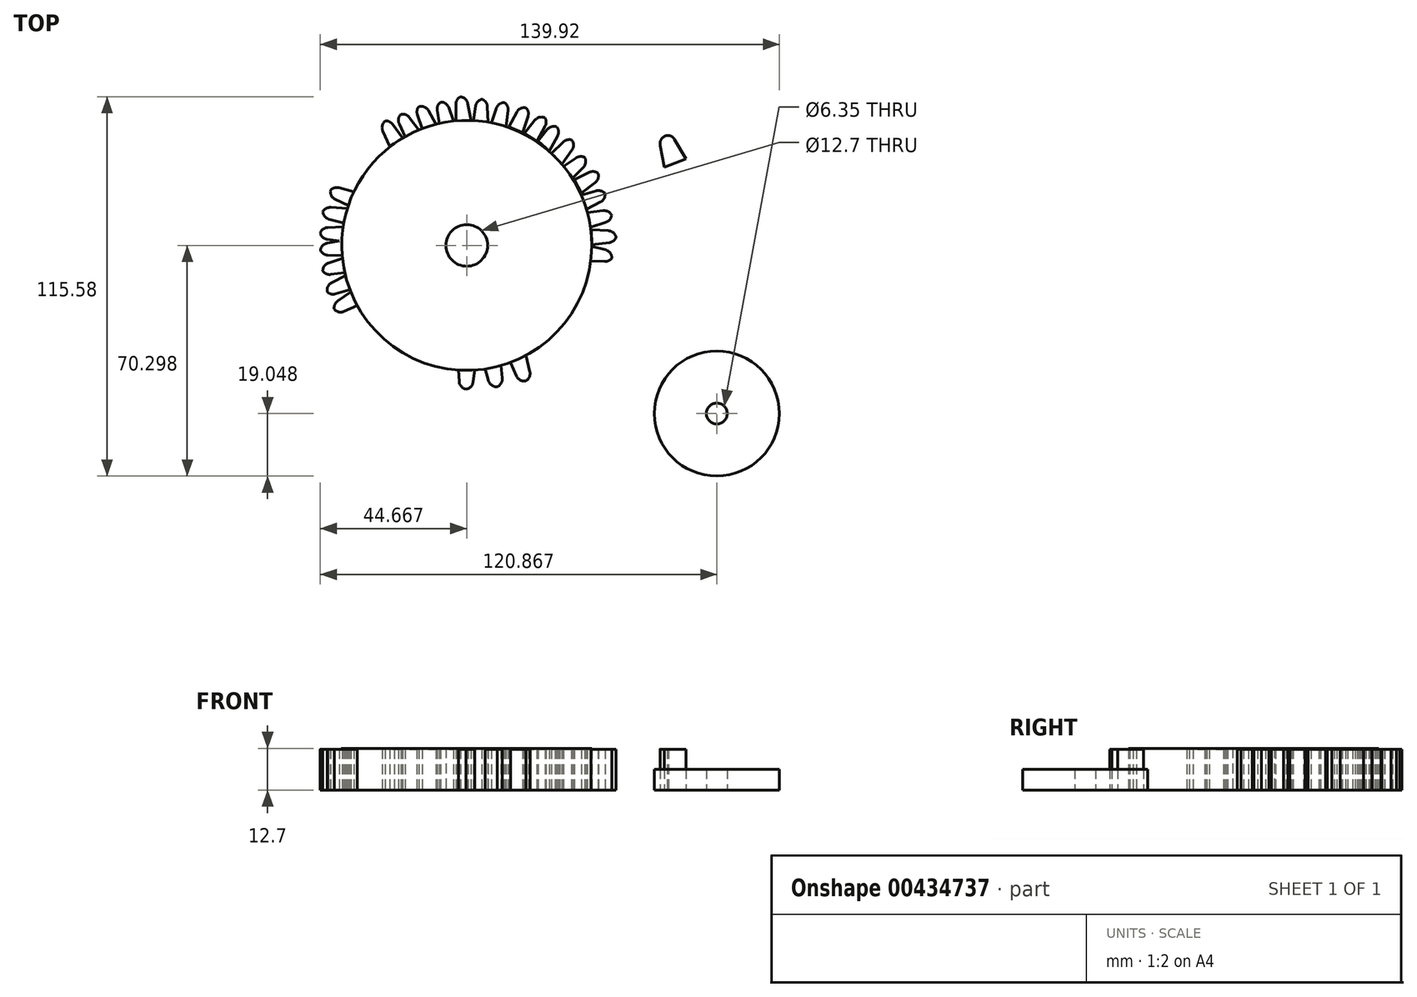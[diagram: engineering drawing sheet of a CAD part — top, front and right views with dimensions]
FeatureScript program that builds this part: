
annotation { "Feature Type Name" : "Feature", "Feature Type Description" : "" }
export const myFeature = defineFeature(function(context is Context, id is Id, definition is map)
    precondition{}
    {
        {
            var Q0;
            Q0=qCreatedBy(makeId("Top.planeOp"),FACE);
            var sketch = newSketch(context, id + "F0", { "sketchPlane" : qUnion([Q0])});
            skCircle(sketch, "E0", {"center": v(-39.08, 21.94) * mm, "radius": 38.1 * mm});
            skCircle(sketch, "E1", {"center": v(-39.08, 21.94) * mm, "radius": 6.35 * mm});
            skSolve(sketch);
        }
        {
            var Q0;
            Q0=makeQuery(id+"F0.imprint","IMPRINT",FACE,{"disambiguationData":[TD([[makeQuery(id+"F0.imprint","IMPRINT",EDGE,{"derivedFrom":sQuery(id+"F0.wireOp",EDGE,"E0")}),1.0]])]});
            extrude(context, id + "F1", {"entities" : qUnion([Q0]), "depth" : 12.7 * mm});
        }
        {
            var Q0;
            Q0=qCreatedBy(makeId("Top.planeOp"),FACE);
            var sketch = newSketch(context, id + "F2", { "sketchPlane" : qUnion([Q0])});
            skCircle(sketch, "E2", {"center": v(37.12, -29.31) * mm, "radius": 19.05 * mm});
            skCircle(sketch, "E3", {"center": v(37.12, -29.31) * mm, "radius": 3.18 * mm});
            skSolve(sketch);
        }
        {
            var Q0;
            Q0=makeQuery(id+"F2.imprint","IMPRINT",FACE,{"disambiguationData":[TD([[makeQuery(id+"F2.imprint","IMPRINT",EDGE,{"derivedFrom":sQuery(id+"F2.wireOp",EDGE,"E2")}),1.0]])]});
            extrude(context, id + "F3", {"entities" : qUnion([Q0]), "depth" : 6.35 * mm});
        }
        {
            var Q0;
            Q0=qCreatedBy(makeId("Top.planeOp"),FACE);
            var sketch = newSketch(context, id + "F4", { "sketchPlane" : qUnion([Q0])});
            skLineSegment(sketch, "E4", {"start": v(-35.3, 66.23) * mm, "end": v(-34.44, 66.16) * mm});
            skLineSegment(sketch, "E5", {"start": v(-32.8, 64.2) * mm, "end": v(-32.6, 58.88) * mm});
            skLineSegment(sketch, "E6", {"start": v(-32.6, 58.88) * mm, "end": v(-37.18, 59.33) * mm});
            skLineSegment(sketch, "E7", {"start": v(-37.18, 59.33) * mm, "end": v(-36.4, 64.4) * mm});
            skPoint(sketch, "E8.visualSharp", {"position": v(-36.84, 66.37) * mm});
            skArc(sketch, "E8.filletArc", {"start": v(-33.64, 66.57) * mm, "mid": v(-35.45, 66.03) * mm, "end": v(-36.4, 64.4) * mm});
            skPoint(sketch, "E9.visualSharp", {"position": v(-33.04, 66.03) * mm});
            skArc(sketch, "E9.filletArc", {"start": v(-32.8, 64.2) * mm, "mid": v(-33.5, 65.87) * mm, "end": v(-35.14, 66.66) * mm});
            skLineSegment(sketch, "E10.MirrorCS", {"start": v(-36.5, -14.4) * mm, "end": v(-41.75, -14.4) * mm});
            skLineSegment(sketch, "E11.MirrorCS", {"start": v(-37.17, -19.67) * mm, "end": v(-36.5, -14.4) * mm});
            skLineSegment(sketch, "E12.MirrorCS", {"start": v(-41.75, -14.4) * mm, "end": v(-41.42, -19.52) * mm});
            skArc(sketch, "E13.MirrorCS", {"start": v(-38.85, -21.92) * mm, "mid": v(-40.6, -21.22) * mm, "end": v(-41.42, -19.52) * mm});
            skArc(sketch, "E14.MirrorCS", {"start": v(-37.17, -19.67) * mm, "mid": v(-38.02, -21.28) * mm, "end": v(-39.71, -21.92) * mm});
            skLineSegment(sketch, "E15", {"start": v(22.03, 55.48) * mm, "end": v(22.39, 55.48) * mm});
            skLineSegment(sketch, "E16", {"start": v(24.23, 54.24) * mm, "end": v(27.77, 48.34) * mm});
            skLineSegment(sketch, "E17", {"start": v(27.77, 48.34) * mm, "end": v(21.15, 45.8) * mm});
            skLineSegment(sketch, "E18", {"start": v(21.15, 45.8) * mm, "end": v(19.87, 52.43) * mm});
            skPoint(sketch, "E19.visualSharp", {"position": v(19.27, 55.48) * mm});
            skArc(sketch, "E19.filletArc", {"start": v(22.39, 55.48) * mm, "mid": v(20.4, 54.55) * mm, "end": v(19.87, 52.43) * mm});
            skPoint(sketch, "E20.visualSharp", {"position": v(23.48, 55.48) * mm});
            skArc(sketch, "E20.filletArc", {"start": v(24.23, 54.24) * mm, "mid": v(23.3, 55.15) * mm, "end": v(22.03, 55.48) * mm});
            skLineSegment(sketch, "E21", {"start": v(-28.47, 65.32) * mm, "end": v(-27.63, 65.13) * mm});
            skLineSegment(sketch, "E22", {"start": v(-26.48, 63) * mm, "end": v(-27.17, 57.73) * mm});
            skLineSegment(sketch, "E23", {"start": v(-27.17, 57.73) * mm, "end": v(-31.65, 58.88) * mm});
            skLineSegment(sketch, "E24", {"start": v(-31.65, 58.88) * mm, "end": v(-30.03, 63.75) * mm});
            skPoint(sketch, "E25.visualSharp", {"position": v(-29.98, 65.66) * mm});
            skArc(sketch, "E25.filletArc", {"start": v(-26.94, 65.43) * mm, "mid": v(-28.82, 65.2) * mm, "end": v(-30.03, 63.75) * mm});
            skPoint(sketch, "E26.visualSharp", {"position": v(-26.26, 64.82) * mm});
            skArc(sketch, "E26.filletArc", {"start": v(-26.48, 63) * mm, "mid": v(-26.9, 64.78) * mm, "end": v(-28.37, 65.83) * mm});
            skLineSegment(sketch, "E27", {"start": v(-21.5, 63.19) * mm, "end": v(-20.68, 62.9) * mm});
            skLineSegment(sketch, "E28", {"start": v(-20.42, 61.32) * mm, "end": v(-22.04, 56.25) * mm});
            skLineSegment(sketch, "E29", {"start": v(-22.04, 56.25) * mm, "end": v(-26.3, 58.08) * mm});
            skLineSegment(sketch, "E30", {"start": v(-26.3, 58.08) * mm, "end": v(-23.83, 62.6) * mm});
            skPoint(sketch, "E31.visualSharp", {"position": v(-22.95, 63.72) * mm});
            skArc(sketch, "E31.filletArc", {"start": v(-20.5, 63.7) * mm, "mid": v(-22.38, 63.8) * mm, "end": v(-23.83, 62.6) * mm});
            skPoint(sketch, "E32.visualSharp", {"position": v(-19.37, 62.42) * mm});
            skArc(sketch, "E32.filletArc", {"start": v(-20.42, 61.32) * mm, "mid": v(-20.52, 63.14) * mm, "end": v(-21.78, 64.43) * mm});
            skLineSegment(sketch, "E33.MirrorCS", {"start": v(-21.04, -11.39) * mm, "end": v(-25.98, -13.19) * mm});
            skLineSegment(sketch, "E34.MirrorCS", {"start": v(-19.87, -16.58) * mm, "end": v(-21.04, -11.39) * mm});
            skLineSegment(sketch, "E35.MirrorCS", {"start": v(-25.98, -13.19) * mm, "end": v(-23.91, -17.89) * mm});
            skPoint(sketch, "E36.MirrorP", {"position": v(-22.95, -20.1) * mm});
            skArc(sketch, "E37.MirrorCS", {"start": v(-20.68, -19.27) * mm, "mid": v(-22.57, -19.22) * mm, "end": v(-23.91, -17.89) * mm});
            skArc(sketch, "E38.MirrorCS", {"start": v(-19.87, -16.58) * mm, "mid": v(-20.12, -18.38) * mm, "end": v(-21.5, -19.56) * mm});
            skLineSegment(sketch, "E39.MirrorCS", {"start": v(-28.77, -13.24) * mm, "end": v(-33.9, -14.4) * mm});
            skLineSegment(sketch, "E40.MirrorCS", {"start": v(-33.9, -14.4) * mm, "end": v(-32.45, -19.32) * mm});
            skLineSegment(sketch, "E41.MirrorCS", {"start": v(-28.26, -18.54) * mm, "end": v(-28.77, -13.24) * mm});
            skArc(sketch, "E42.MirrorCS", {"start": v(-28.26, -18.54) * mm, "mid": v(-28.74, -20.3) * mm, "end": v(-30.26, -21.29) * mm});
            skArc(sketch, "E43.MirrorCS", {"start": v(-29.42, -21.1) * mm, "mid": v(-31.29, -20.8) * mm, "end": v(-32.45, -19.32) * mm});
            skLineSegment(sketch, "E44", {"start": v(-14.43, 59.39) * mm, "end": v(-13.73, 58.9) * mm});
            skLineSegment(sketch, "E45", {"start": v(-15.19, 58.33) * mm, "end": v(-17.67, 53.62) * mm});
            skLineSegment(sketch, "E46", {"start": v(-17.67, 53.62) * mm, "end": v(-21.55, 56.1) * mm});
            skLineSegment(sketch, "E47", {"start": v(-21.55, 56.1) * mm, "end": v(-18.33, 60.1) * mm});
            skPoint(sketch, "E48.visualSharp", {"position": v(-15.7, 60.27) * mm});
            skArc(sketch, "E48.filletArc", {"start": v(-14.86, 60.6) * mm, "mid": v(-16.7, 61.04) * mm, "end": v(-18.33, 60.1) * mm});
            skPoint(sketch, "E49.visualSharp", {"position": v(-12.58, 58.09) * mm});
            skArc(sketch, "E49.filletArc", {"start": v(-15.19, 58.33) * mm, "mid": v(-14.96, 60.13) * mm, "end": v(-15.99, 61.63) * mm});
            skLineSegment(sketch, "E50", {"start": v(-42.6, 66.02) * mm, "end": v(-41.75, 66.1) * mm});
            skLineSegment(sketch, "E51", {"start": v(-38.81, 65.23) * mm, "end": v(-37.73, 60.09) * mm});
            skLineSegment(sketch, "E52", {"start": v(-37.73, 60.09) * mm, "end": v(-42.34, 59.84) * mm});
            skLineSegment(sketch, "E53", {"start": v(-42.34, 59.84) * mm, "end": v(-42.41, 64.91) * mm});
            skPoint(sketch, "E54.visualSharp", {"position": v(-44.12, 65.9) * mm});
            skArc(sketch, "E54.filletArc", {"start": v(-40.09, 67.48) * mm, "mid": v(-41.76, 66.66) * mm, "end": v(-42.41, 64.91) * mm});
            skPoint(sketch, "E55.visualSharp", {"position": v(-40.37, 66.2) * mm});
            skArc(sketch, "E55.filletArc", {"start": v(-38.81, 65.23) * mm, "mid": v(-39.77, 66.74) * mm, "end": v(-41.5, 67.23) * mm});
            skLineSegment(sketch, "E56", {"start": v(-49.7, 65.98) * mm, "end": v(-48.86, 66.16) * mm});
            skLineSegment(sketch, "E57", {"start": v(-44.58, 63.95) * mm, "end": v(-42.78, 59.01) * mm});
            skLineSegment(sketch, "E58", {"start": v(-42.78, 59.01) * mm, "end": v(-47.28, 58.17) * mm});
            skLineSegment(sketch, "E59", {"start": v(-47.28, 58.17) * mm, "end": v(-48.09, 63.18) * mm});
            skPoint(sketch, "E60.visualSharp", {"position": v(-51.18, 65.64) * mm});
            skArc(sketch, "E60.filletArc", {"start": v(-46.15, 66.05) * mm, "mid": v(-47.69, 65) * mm, "end": v(-48.09, 63.18) * mm});
            skPoint(sketch, "E61.visualSharp", {"position": v(-47.51, 66.47) * mm});
            skArc(sketch, "E61.filletArc", {"start": v(-44.58, 63.95) * mm, "mid": v(-45.75, 65.3) * mm, "end": v(-47.52, 65.55) * mm});
            skLineSegment(sketch, "E62", {"start": v(-55.81, 62.91) * mm, "end": v(-55.02, 63.2) * mm});
            skLineSegment(sketch, "E63", {"start": v(-50.75, 63.05) * mm, "end": v(-48.18, 58.47) * mm});
            skLineSegment(sketch, "E64", {"start": v(-48.18, 58.47) * mm, "end": v(-52.55, 57.03) * mm});
            skLineSegment(sketch, "E65", {"start": v(-52.55, 57.03) * mm, "end": v(-54.15, 61.84) * mm});
            skPoint(sketch, "E66.visualSharp", {"position": v(-57.25, 62.4) * mm});
            skArc(sketch, "E66.filletArc", {"start": v(-52.7, 64.98) * mm, "mid": v(-54.05, 63.7) * mm, "end": v(-54.15, 61.84) * mm});
            skPoint(sketch, "E67.visualSharp", {"position": v(-53.72, 63.68) * mm});
            skArc(sketch, "E67.filletArc", {"start": v(-50.75, 63.05) * mm, "mid": v(-52.12, 64.2) * mm, "end": v(-53.91, 64.15) * mm});
            skLineSegment(sketch, "E68", {"start": v(-62.7, 59.48) * mm, "end": v(-61.97, 59.9) * mm});
            skLineSegment(sketch, "E69", {"start": v(-56.56, 60.92) * mm, "end": v(-53.44, 56.7) * mm});
            skLineSegment(sketch, "E70", {"start": v(-53.44, 56.7) * mm, "end": v(-57.76, 54.9) * mm});
            skLineSegment(sketch, "E71", {"start": v(-57.76, 54.9) * mm, "end": v(-59.69, 58.95) * mm});
            skPoint(sketch, "E72.visualSharp", {"position": v(-64.04, 58.73) * mm});
            skArc(sketch, "E72.filletArc", {"start": v(-59.13, 61.9) * mm, "mid": v(-59.89, 60.51) * mm, "end": v(-59.69, 58.95) * mm});
            skArc(sketch, "E73.filletArc", {"start": v(-56.56, 60.92) * mm, "mid": v(-58.06, 61.9) * mm, "end": v(-59.83, 61.63) * mm});
            skPoint(sketch, "E74", {"position": v(-58.06, 61.9) * mm});
            skLineSegment(sketch, "E75", {"start": v(-76.83, 45.84) * mm, "end": v(-76.38, 46.56) * mm});
            skLineSegment(sketch, "E76", {"start": v(-81.45, 27.4) * mm, "end": v(-76.13, 27.64) * mm});
            skLineSegment(sketch, "E77", {"start": v(-76.13, 27.64) * mm, "end": v(-76.55, 23.05) * mm});
            skLineSegment(sketch, "E78", {"start": v(-76.55, 23.05) * mm, "end": v(-81.64, 23.8) * mm});
            skPoint(sketch, "E79.visualSharp", {"position": v(-77.65, 44.52) * mm});
            skArc(sketch, "E79.filletArc", {"start": v(-83.82, 26.55) * mm, "mid": v(-83.27, 24.74) * mm, "end": v(-81.64, 23.8) * mm});
            skPoint(sketch, "E80.visualSharp", {"position": v(-75.64, 47.76) * mm});
            skArc(sketch, "E80.filletArc", {"start": v(-81.45, 27.4) * mm, "mid": v(-83.12, 26.69) * mm, "end": v(-83.9, 25.05) * mm});
            skLineSegment(sketch, "E81", {"start": v(-72.93, 51.51) * mm, "end": v(-72.38, 52.17) * mm});
            skLineSegment(sketch, "E82", {"start": v(-80.54, 33.53) * mm, "end": v(-75.23, 33.12) * mm});
            skLineSegment(sketch, "E83", {"start": v(-75.23, 33.12) * mm, "end": v(-76.13, 28.58) * mm});
            skLineSegment(sketch, "E84", {"start": v(-76.13, 28.58) * mm, "end": v(-81.09, 29.94) * mm});
            skPoint(sketch, "E85.visualSharp", {"position": v(-73.92, 50.32) * mm});
            skArc(sketch, "E85.filletArc", {"start": v(-82.92, 32.93) * mm, "mid": v(-82.6, 31.07) * mm, "end": v(-81.09, 29.94) * mm});
            skPoint(sketch, "E86.visualSharp", {"position": v(-71.49, 53.25) * mm});
            skArc(sketch, "E86.filletArc", {"start": v(-80.54, 33.53) * mm, "mid": v(-82.28, 33.02) * mm, "end": v(-83.25, 31.48) * mm});
            skLineSegment(sketch, "E87", {"start": v(-80.22, 38.77) * mm, "end": v(-79.97, 39.6) * mm});
            skLineSegment(sketch, "E88", {"start": v(-78.12, 39.49) * mm, "end": v(-72.97, 38.14) * mm});
            skLineSegment(sketch, "E89", {"start": v(-72.97, 38.14) * mm, "end": v(-74.57, 33.8) * mm});
            skLineSegment(sketch, "E90", {"start": v(-74.57, 33.8) * mm, "end": v(-79.2, 36.01) * mm});
            skPoint(sketch, "E91.visualSharp", {"position": v(-80.67, 37.3) * mm});
            skArc(sketch, "E91.filletArc", {"start": v(-80.48, 39.29) * mm, "mid": v(-80.5, 37.4) * mm, "end": v(-79.2, 36.01) * mm});
            skPoint(sketch, "E92.visualSharp", {"position": v(-79.57, 40.94) * mm});
            skArc(sketch, "E92.filletArc", {"start": v(-78.12, 39.49) * mm, "mid": v(-79.93, 39.3) * mm, "end": v(-81.15, 37.96) * mm});
            skLineSegment(sketch, "E93", {"start": v(-61.28, 61.34) * mm, "end": v(-60.53, 61.74) * mm});
            skLineSegment(sketch, "E94", {"start": v(-61.67, 58.84) * mm, "end": v(-58.6, 54.5) * mm});
            skLineSegment(sketch, "E95", {"start": v(-58.6, 54.5) * mm, "end": v(-62.57, 52.16) * mm});
            skLineSegment(sketch, "E96", {"start": v(-62.57, 52.16) * mm, "end": v(-64.68, 56.84) * mm});
            skPoint(sketch, "E97.visualSharp", {"position": v(-62.65, 60.61) * mm});
            skArc(sketch, "E97.filletArc", {"start": v(-63.55, 60.16) * mm, "mid": v(-64.78, 58.72) * mm, "end": v(-64.68, 56.84) * mm});
            skPoint(sketch, "E98.visualSharp", {"position": v(-59.29, 62.4) * mm});
            skArc(sketch, "E98.filletArc", {"start": v(-61.67, 58.84) * mm, "mid": v(-63.18, 59.85) * mm, "end": v(-64.98, 59.62) * mm});
            skLineSegment(sketch, "E99", {"start": v(-83.05, 19.12) * mm, "end": v(-83.1, 19.97) * mm});
            skLineSegment(sketch, "E100", {"start": v(-81.64, 22.6) * mm, "end": v(-76.46, 23.5) * mm});
            skLineSegment(sketch, "E101", {"start": v(-76.46, 23.5) * mm, "end": v(-76.37, 18.9) * mm});
            skLineSegment(sketch, "E102", {"start": v(-76.37, 18.9) * mm, "end": v(-81.44, 18.98) * mm});
            skPoint(sketch, "E103.visualSharp", {"position": v(-80.53, 37.82) * mm});
            skArc(sketch, "E103.filletArc", {"start": v(-83.93, 21.4) * mm, "mid": v(-83.16, 19.7) * mm, "end": v(-81.44, 18.98) * mm});
            skPoint(sketch, "E104.visualSharp", {"position": v(-83.16, 21.35) * mm});
            skArc(sketch, "E104.filletArc", {"start": v(-81.64, 22.6) * mm, "mid": v(-83.18, 21.68) * mm, "end": v(-83.73, 19.98) * mm});
            skLineSegment(sketch, "E105", {"start": v(-83.13, 32.89) * mm, "end": v(-82.92, 33.7) * mm});
            skLineSegment(sketch, "E106", {"start": v(-81.21, 16.6) * mm, "end": v(-76.22, 18.24) * mm});
            skLineSegment(sketch, "E107", {"start": v(-76.22, 18.24) * mm, "end": v(-75.53, 13.7) * mm});
            skLineSegment(sketch, "E108", {"start": v(-75.53, 13.7) * mm, "end": v(-80.56, 13.07) * mm});
            skPoint(sketch, "E109.visualSharp", {"position": v(-83.5, 31.4) * mm});
            skArc(sketch, "E109.filletArc", {"start": v(-83.36, 15.1) * mm, "mid": v(-82.36, 13.54) * mm, "end": v(-80.56, 13.07) * mm});
            skPoint(sketch, "E110.visualSharp", {"position": v(-82.58, 35.05) * mm});
            skArc(sketch, "E110.filletArc", {"start": v(-81.21, 16.6) * mm, "mid": v(-82.6, 15.49) * mm, "end": v(-82.91, 13.72) * mm});
            skLineSegment(sketch, "E111", {"start": v(-83.17, 26.04) * mm, "end": v(-83.07, 26.88) * mm});
            skLineSegment(sketch, "E112", {"start": v(-80.26, 10.6) * mm, "end": v(-75.6, 13.02) * mm});
            skLineSegment(sketch, "E113", {"start": v(-75.6, 13.02) * mm, "end": v(-74.3, 8.6) * mm});
            skLineSegment(sketch, "E114", {"start": v(-74.3, 8.6) * mm, "end": v(-79.17, 7.16) * mm});
            skPoint(sketch, "E115.visualSharp", {"position": v(-83.35, 24.52) * mm});
            skArc(sketch, "E115.filletArc", {"start": v(-82.26, 8.72) * mm, "mid": v(-81.02, 7.33) * mm, "end": v(-79.17, 7.16) * mm});
            skPoint(sketch, "E116.visualSharp", {"position": v(-82.9, 28.25) * mm});
            skArc(sketch, "E116.filletArc", {"start": v(-80.26, 10.6) * mm, "mid": v(-81.46, 9.27) * mm, "end": v(-81.47, 7.48) * mm});
            skLineSegment(sketch, "E117", {"start": v(-83.23, 18.33) * mm, "end": v(-83.26, 19.18) * mm});
            skLineSegment(sketch, "E118", {"start": v(-78.42, 5) * mm, "end": v(-74.1, 7.97) * mm});
            skLineSegment(sketch, "E119", {"start": v(-74.1, 7.97) * mm, "end": v(-72.45, 3.6) * mm});
            skLineSegment(sketch, "E120", {"start": v(-72.45, 3.6) * mm, "end": v(-76.56, 1.8) * mm});
            skPoint(sketch, "E121.visualSharp", {"position": v(-83.17, 16.81) * mm});
            skArc(sketch, "E121.filletArc", {"start": v(-79.48, 2.46) * mm, "mid": v(-78.13, 1.65) * mm, "end": v(-76.56, 1.8) * mm});
            skArc(sketch, "E122.filletArc", {"start": v(-78.42, 5) * mm, "mid": v(-79.44, 3.52) * mm, "end": v(-79.24, 1.74) * mm});
            skPoint(sketch, "E123", {"position": v(-83.28, 23.57) * mm});
            skLineSegment(sketch, "E124.0", {"start": v(-83.76, 22.62) * mm, "end": v(-83.28, 23.57) * mm, "construction": true});
            skLineSegment(sketch, "E125.0", {"start": v(-69.32, 44.87) * mm, "end": v(-69.02, 45.47) * mm, "construction": true});
            skLineSegment(sketch, "E126", {"start": v(2.46, 38.33) * mm, "end": v(2.76, 37.52) * mm});
            skLineSegment(sketch, "E127", {"start": v(1.68, 35.2) * mm, "end": v(-3.04, 32.75) * mm});
            skLineSegment(sketch, "E128", {"start": v(-3.04, 32.75) * mm, "end": v(-4.6, 37.1) * mm});
            skLineSegment(sketch, "E129", {"start": v(-4.6, 37.1) * mm, "end": v(0.34, 38.55) * mm});
            skPoint(sketch, "E130.visualSharp", {"position": v(1.92, 39.78) * mm});
            skArc(sketch, "E130.filletArc", {"start": v(3.47, 36.98) * mm, "mid": v(2.22, 38.38) * mm, "end": v(0.34, 38.55) * mm});
            skPoint(sketch, "E131.visualSharp", {"position": v(3.24, 36.2) * mm});
            skArc(sketch, "E131.filletArc", {"start": v(1.68, 35.2) * mm, "mid": v(2.9, 36.55) * mm, "end": v(2.91, 38.37) * mm});
            skLineSegment(sketch, "E132", {"start": v(4.54, 31.76) * mm, "end": v(4.73, 30.92) * mm});
            skLineSegment(sketch, "E133", {"start": v(3.3, 28.98) * mm, "end": v(-1.77, 27.35) * mm});
            skLineSegment(sketch, "E134", {"start": v(-1.77, 27.35) * mm, "end": v(-2.64, 31.9) * mm});
            skLineSegment(sketch, "E135", {"start": v(-2.64, 31.9) * mm, "end": v(2.46, 32.5) * mm});
            skPoint(sketch, "E136.visualSharp", {"position": v(4.2, 33.27) * mm});
            skArc(sketch, "E136.filletArc", {"start": v(5.29, 30.43) * mm, "mid": v(4.29, 32.03) * mm, "end": v(2.46, 32.5) * mm});
            skPoint(sketch, "E137.visualSharp", {"position": v(5.04, 29.55) * mm});
            skArc(sketch, "E137.filletArc", {"start": v(3.3, 28.98) * mm, "mid": v(4.72, 30.1) * mm, "end": v(5.04, 31.9) * mm});
            skLineSegment(sketch, "E138", {"start": v(5.59, 24.54) * mm, "end": v(5.67, 23.69) * mm});
            skLineSegment(sketch, "E139", {"start": v(4.36, 22.78) * mm, "end": v(-0.92, 22.09) * mm});
            skLineSegment(sketch, "E140", {"start": v(-0.92, 22.09) * mm, "end": v(-1.08, 26.71) * mm});
            skLineSegment(sketch, "E141", {"start": v(-1.08, 26.71) * mm, "end": v(4.05, 26.4) * mm});
            skPoint(sketch, "E142.visualSharp", {"position": v(5.45, 26.08) * mm});
            skArc(sketch, "E142.filletArc", {"start": v(6.47, 23.86) * mm, "mid": v(5.76, 25.61) * mm, "end": v(4.05, 26.4) * mm});
            skPoint(sketch, "E143.visualSharp", {"position": v(5.8, 22.3) * mm});
            skArc(sketch, "E143.filletArc", {"start": v(4.36, 22.78) * mm, "mid": v(5.96, 23.64) * mm, "end": v(6.59, 25.34) * mm});
            skLineSegment(sketch, "E144", {"start": v(5.16, 16.54) * mm, "end": v(5.01, 15.69) * mm});
            skLineSegment(sketch, "E145", {"start": v(2.9, 17) * mm, "end": v(-2.41, 17.24) * mm});
            skLineSegment(sketch, "E146", {"start": v(-2.41, 17.24) * mm, "end": v(-1.82, 21.81) * mm});
            skLineSegment(sketch, "E147", {"start": v(-1.82, 21.81) * mm, "end": v(3.18, 20.61) * mm});
            skPoint(sketch, "E148.visualSharp", {"position": v(5.42, 18.06) * mm});
            skArc(sketch, "E148.filletArc", {"start": v(5.1, 17.68) * mm, "mid": v(4.72, 19.53) * mm, "end": v(3.18, 20.61) * mm});
            skPoint(sketch, "E149.visualSharp", {"position": v(4.77, 14.3) * mm});
            skArc(sketch, "E149.filletArc", {"start": v(2.9, 17) * mm, "mid": v(4.63, 17.57) * mm, "end": v(5.55, 19.14) * mm});
            skLineSegment(sketch, "E150", {"start": v(-0.84, 44.84) * mm, "end": v(-0.42, 44.1) * mm});
            skLineSegment(sketch, "E151", {"start": v(0.05, 41.08) * mm, "end": v(-4.14, 37.92) * mm});
            skLineSegment(sketch, "E152", {"start": v(-4.14, 37.92) * mm, "end": v(-6.32, 41.98) * mm});
            skLineSegment(sketch, "E153", {"start": v(-6.32, 41.98) * mm, "end": v(-1.77, 44.2) * mm});
            skPoint(sketch, "E154.visualSharp", {"position": v(-1.6, 46.17) * mm});
            skArc(sketch, "E154.filletArc", {"start": v(1.54, 43.2) * mm, "mid": v(0.09, 44.35) * mm, "end": v(-1.77, 44.2) * mm});
            skPoint(sketch, "E155.visualSharp", {"position": v(0.27, 42.9) * mm});
            skArc(sketch, "E155.filletArc", {"start": v(0.05, 41.08) * mm, "mid": v(1, 42.6) * mm, "end": v(0.72, 44.36) * mm});
            skLineSegment(sketch, "E156", {"start": v(-3.9, 51.24) * mm, "end": v(-3.38, 50.58) * mm});
            skLineSegment(sketch, "E157", {"start": v(-3.56, 45.75) * mm, "end": v(-7.26, 42.02) * mm});
            skLineSegment(sketch, "E158", {"start": v(-7.26, 42.02) * mm, "end": v(-9.94, 45.74) * mm});
            skLineSegment(sketch, "E159", {"start": v(-9.94, 45.74) * mm, "end": v(-5.75, 48.6) * mm});
            skPoint(sketch, "E160.visualSharp", {"position": v(-4.85, 52.44) * mm});
            skArc(sketch, "E160.filletArc", {"start": v(-2.33, 48.07) * mm, "mid": v(-3.94, 49.01) * mm, "end": v(-5.75, 48.6) * mm});
            skPoint(sketch, "E161.visualSharp", {"position": v(-2.53, 49.48) * mm});
            skArc(sketch, "E161.filletArc", {"start": v(-3.56, 45.75) * mm, "mid": v(-2.83, 47.39) * mm, "end": v(-3.37, 49.1) * mm});
            skLineSegment(sketch, "E162", {"start": v(-9.28, 55.48) * mm, "end": v(-8.68, 54.88) * mm});
            skLineSegment(sketch, "E163", {"start": v(-7, 50.95) * mm, "end": v(-10.05, 46.67) * mm});
            skLineSegment(sketch, "E164", {"start": v(-10.05, 46.67) * mm, "end": v(-13.22, 50.02) * mm});
            skLineSegment(sketch, "E165", {"start": v(-13.22, 50.02) * mm, "end": v(-9.55, 53.52) * mm});
            skPoint(sketch, "E166.visualSharp", {"position": v(-10.37, 56.55) * mm});
            skArc(sketch, "E166.filletArc", {"start": v(-6.1, 53.54) * mm, "mid": v(-7.83, 54.21) * mm, "end": v(-9.55, 53.52) * mm});
            skPoint(sketch, "E167.visualSharp", {"position": v(-7.7, 53.9) * mm});
            skArc(sketch, "E167.filletArc", {"start": v(-7, 50.95) * mm, "mid": v(-6.55, 52.69) * mm, "end": v(-7.36, 54.28) * mm});
            skLineSegment(sketch, "E168", {"start": v(-15.37, 59.96) * mm, "end": v(-14.68, 59.47) * mm});
            skLineSegment(sketch, "E169", {"start": v(-11.4, 55.3) * mm, "end": v(-13.9, 50.68) * mm});
            skLineSegment(sketch, "E170", {"start": v(-13.9, 50.68) * mm, "end": v(-17.35, 53.82) * mm});
            skLineSegment(sketch, "E171", {"start": v(-17.35, 53.82) * mm, "end": v(-14.52, 57.3) * mm});
            skPoint(sketch, "E172.visualSharp", {"position": v(-16.61, 60.85) * mm});
            skArc(sketch, "E172.filletArc", {"start": v(-11.62, 58.04) * mm, "mid": v(-13.2, 58.14) * mm, "end": v(-14.52, 57.3) * mm});
            skArc(sketch, "E173.filletArc", {"start": v(-11.4, 55.3) * mm, "mid": v(-11.17, 57.08) * mm, "end": v(-12.16, 58.57) * mm});
            skPoint(sketch, "E174", {"position": v(-11.17, 57.08) * mm});
            skLineSegment(sketch, "E175.0", {"start": v(-11.62, 58.04) * mm, "end": v(-11.17, 57.08) * mm, "construction": true});
            skLineSegment(sketch, "E176.0", {"start": v(-3.04, 32.75) * mm, "end": v(-2.64, 31.9) * mm, "construction": true});
            skPoint(sketch, "E177", {"position": v(-39, 21.81) * mm});
            skLineSegment(sketch, "E178", {"start": v(-39, 21.81) * mm, "end": v(-92.89, 21.81) * mm});
            skLineSegment(sketch, "E179", {"start": v(-92.89, 21.81) * mm, "end": v(-39, 21.81) * mm});
            skLineSegment(sketch, "E180", {"start": v(-39, 21.81) * mm, "end": v(11.45, 20.84) * mm});
            skSolve(sketch);
        }
        {
            var Q0;
            Q0 = qSketchRegion(id + "F4", true);
            extrude(context, id + "F5", {"entities" : qUnion([Q0]), "operationType" : NewBodyOperationType.ADD, "depth" : 12.45 * mm});
        }
    });
